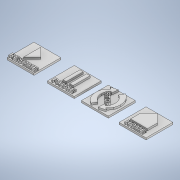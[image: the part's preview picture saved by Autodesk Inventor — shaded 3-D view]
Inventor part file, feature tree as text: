
AUTODESK INVENTOR PART (.ipt)
format: ipt  version: 2022.1 (Build 261234020, 234B)  size: 548,864 bytes
history: native  units: mm
features: extrude x2, sketch x2
ambient origin geometry x8: Origin, YZ Plane, XZ Plane, XY Plane, X Axis, Y Axis, Z Axis, Center Point
bodies: Solido1 (feature_tree)
feature tree (4):
  extrude  "Estrusione1"  Depth=14.5mm
  extrude  "Estrusione2"  Depth=14.5mm
  sketch  "Schizzo1"
  sketch  "Schizzo2"
